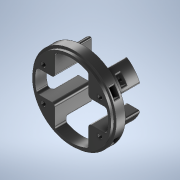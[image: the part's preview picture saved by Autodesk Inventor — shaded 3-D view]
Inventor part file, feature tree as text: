
AUTODESK INVENTOR PART (.ipt)
format: ipt  version: 2020 (Build 240168000, 168)  size: 395,264 bytes
history: native  units: in
note: dims shown in document units (in); Inventor stores cm internally (conversion verified against a paired STEP export)
features: sketch x6, extrude x3, fillet x3, hole x2, mirror x2, revolve x1
ambient origin geometry x8: Origin, YZ Plane, XZ Plane, XY Plane, X Axis, Y Axis, Z Axis, Center Point
bodies: Solid1 (feature_tree)
feature tree (17):
  revolve  "Revolution1"  [1 undecoded]
  extrude  "Extrusion1"  Depth=0.5in
  fillet  "Fillet1"  Radius=1.5in
  hole  "Hole1"  [1 undecoded]
  extrude  "Extrusion2"  Depth=1.5in
  fillet  "Fillet2"  Radius=1.0in
  hole  "Hole2"  [1 undecoded]
  extrude  "Extrusion3"  Depth=0.0625in
  mirror  "Mirror1"
  mirror  "Mirror2"
  fillet  "Fillet3"  Radius=0.125in
  sketch  "Sketch1"  dims[d0=1.74in d1=0.125in]
  sketch  "Sketch2"  dims[d2=1.85in d3=0.5in d5=1.5in]
  sketch  "Sketch4"  dims[d6=1.125in d7=90.0deg]
  sketch  "Sketch5"  dims[d8=3.25in d9=1.5in d10=1.0in]
  sketch  "Sketch6"  dims[d11=0.0in d12=0.0in d18=0.125in]
  sketch  "Sketch7"  dims[d19=0.5312in d20=1.75in d21=0.125in d22=2.5in d23=1.5in d24=0.205in d25=0.75in d26=0.375in d27=0.25in d28=0.5635in d29=0.4375in d30=0.0in d31=0.385in d32=0.25in d33=0.0in d34=0.0312in d35=2.0in d36=1.5in d37=0.205in d38=0.75in d39=0.375in d40=0.25in d41=0.5635in d42=0.75in d43=0.0in d44=0.385in d45=0.25in d46=0.0in d47=0.0625in]
note: 3 required parameter values undecoded (feature->parameter linkage not recoverable at this tier; creation-order binding heuristic only, values carry confidence <= 0.55)